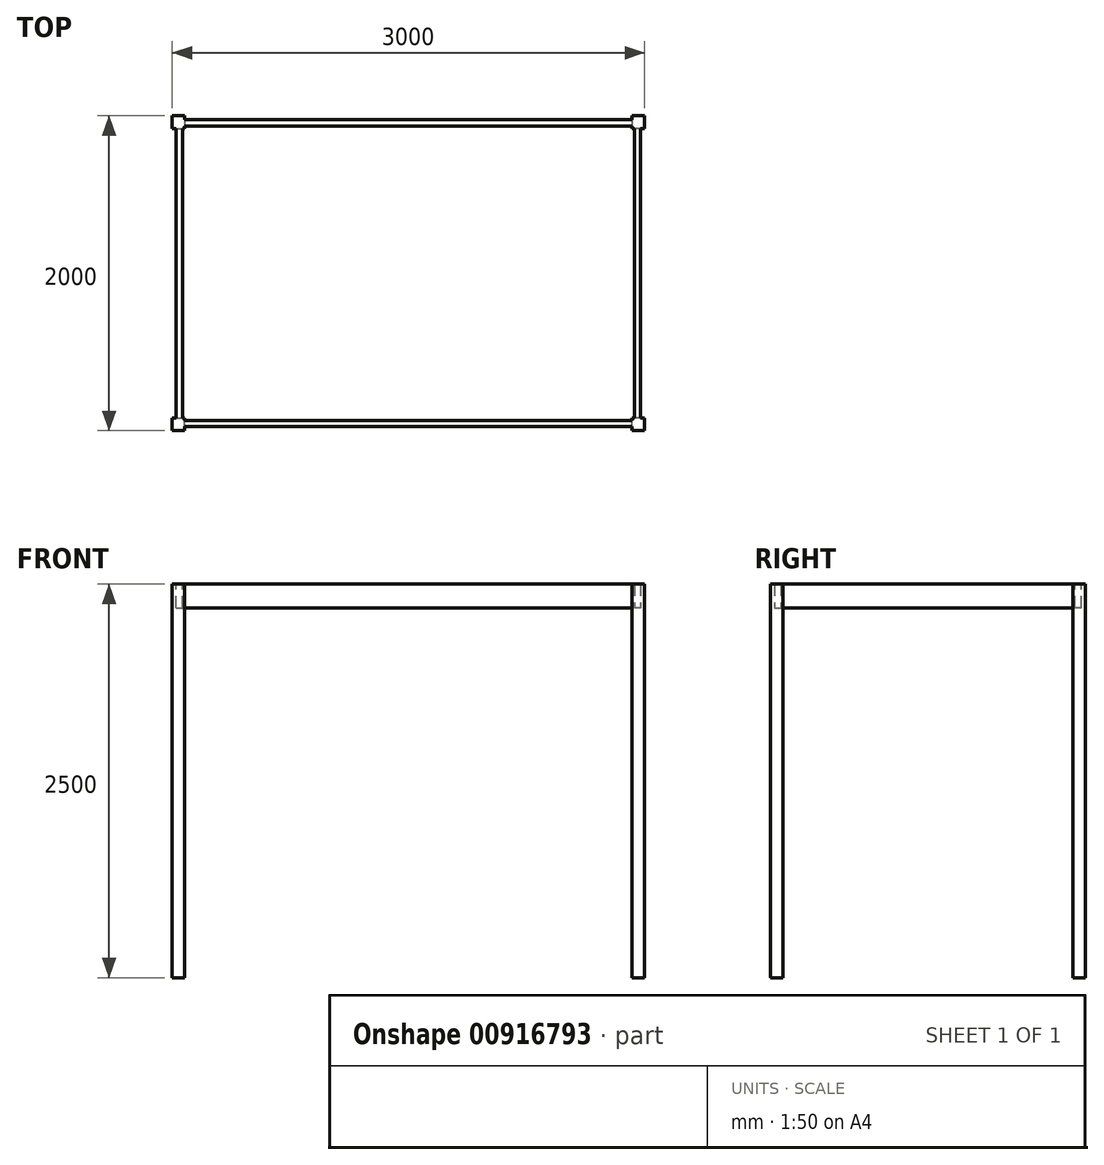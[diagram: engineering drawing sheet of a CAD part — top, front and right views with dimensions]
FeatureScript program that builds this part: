
annotation { "Feature Type Name" : "Feature", "Feature Type Description" : "" }
export const myFeature = defineFeature(function(context is Context, id is Id, definition is map)
    precondition{}
    {
        {
            var Q0;
            Q0=qCreatedBy(makeId("Top.planeOp"),FACE);
            var sketch = newSketch(context, id + "F0", { "sketchPlane" : qUnion([Q0])});
            skLineSegment(sketch, "E0.bottom", {"start": v(1475, 975) * mm, "end": v(-1475, 975) * mm});
            skLineSegment(sketch, "E0.top", {"start": v(1475, -975) * mm, "end": v(-1475, -975) * mm});
            skLineSegment(sketch, "E0.left", {"start": v(1475, 975) * mm, "end": v(1475, -975) * mm});
            skLineSegment(sketch, "E0.right", {"start": v(-1475, 975) * mm, "end": v(-1475, -975) * mm});
            skPoint(sketch, "E0.middle", {"position": v(0, 0) * mm});
            skLineSegment(sketch, "E1.bottom", {"start": v(1435, 935) * mm, "end": v(-1435, 935) * mm});
            skLineSegment(sketch, "E1.top", {"start": v(1435, -935) * mm, "end": v(-1435, -935) * mm});
            skLineSegment(sketch, "E1.left", {"start": v(1435, 935) * mm, "end": v(1435, -935) * mm});
            skLineSegment(sketch, "E1.right", {"start": v(-1435, 935) * mm, "end": v(-1435, -935) * mm});
            skSolve(sketch);
        }
        {
            var Q0;
            Q0=qCreatedBy(makeId("Top.planeOp"),FACE);
            var sketch = newSketch(context, id + "F1", { "sketchPlane" : qUnion([Q0])});
            skLineSegment(sketch, "E2.bottom", {"start": v(1500, 1000) * mm, "end": v(-1500, 1000) * mm, "construction": true});
            skLineSegment(sketch, "E2.top", {"start": v(1500, -1000) * mm, "end": v(-1500, -1000) * mm, "construction": true});
            skLineSegment(sketch, "E2.left", {"start": v(1500, 1000) * mm, "end": v(1500, -1000) * mm, "construction": true});
            skLineSegment(sketch, "E2.right", {"start": v(-1500, 1000) * mm, "end": v(-1500, -1000) * mm, "construction": true});
            skPoint(sketch, "E2.middle", {"position": v(0, 0) * mm});
            skLineSegment(sketch, "E3", {"start": v(-1500, 0) * mm, "end": v(1500, 0) * mm, "construction": true});
            skLineSegment(sketch, "E4", {"start": v(0, 1000) * mm, "end": v(0, -1000) * mm, "construction": true});
            skLineSegment(sketch, "E5.bottom", {"start": v(1500, 1000) * mm, "end": v(1420, 1000) * mm});
            skLineSegment(sketch, "E5.top", {"start": v(1500, 920) * mm, "end": v(1420, 920) * mm});
            skLineSegment(sketch, "E5.left", {"start": v(1500, 1000) * mm, "end": v(1500, 920) * mm});
            skLineSegment(sketch, "E5.right", {"start": v(1420, 1000) * mm, "end": v(1420, 920) * mm});
            skLineSegment(sketch, "E6.bottom", {"start": v(1500, -1000) * mm, "end": v(1420, -1000) * mm});
            skLineSegment(sketch, "E6.top", {"start": v(1500, -920) * mm, "end": v(1420, -920) * mm});
            skLineSegment(sketch, "E6.left", {"start": v(1500, -1000) * mm, "end": v(1500, -920) * mm});
            skLineSegment(sketch, "E6.right", {"start": v(1420, -1000) * mm, "end": v(1420, -920) * mm});
            skLineSegment(sketch, "E7.bottom", {"start": v(-1500, -1000) * mm, "end": v(-1420, -1000) * mm});
            skLineSegment(sketch, "E7.top", {"start": v(-1500, -920) * mm, "end": v(-1420, -920) * mm});
            skLineSegment(sketch, "E7.left", {"start": v(-1500, -1000) * mm, "end": v(-1500, -920) * mm});
            skLineSegment(sketch, "E7.right", {"start": v(-1420, -1000) * mm, "end": v(-1420, -920) * mm});
            skLineSegment(sketch, "E8.bottom", {"start": v(-1500, 1000) * mm, "end": v(-1420, 1000) * mm});
            skLineSegment(sketch, "E8.top", {"start": v(-1500, 920) * mm, "end": v(-1420, 920) * mm});
            skLineSegment(sketch, "E8.left", {"start": v(-1500, 1000) * mm, "end": v(-1500, 920) * mm});
            skLineSegment(sketch, "E8.right", {"start": v(-1420, 1000) * mm, "end": v(-1420, 920) * mm});
            skSolve(sketch);
        }
        {
            var Q0;
            Q0 = qSketchRegion(id + "F0", true);
            extrude(context, id + "F2", {"entities" : qUnion([Q0]), "oppositeDirection" : true, "depth" : 150 * mm, "offsetDistance" : 25 * mm});
        }
        {
            var Q0;
            Q0 = qSketchRegion(id + "F1", true);
            extrude(context, id + "F3", {"entities" : qUnion([Q0]), "operationType" : NewBodyOperationType.ADD, "oppositeDirection" : true, "depth" : 2500 * mm, "offsetDistance" : 25 * mm});
        }
    });
